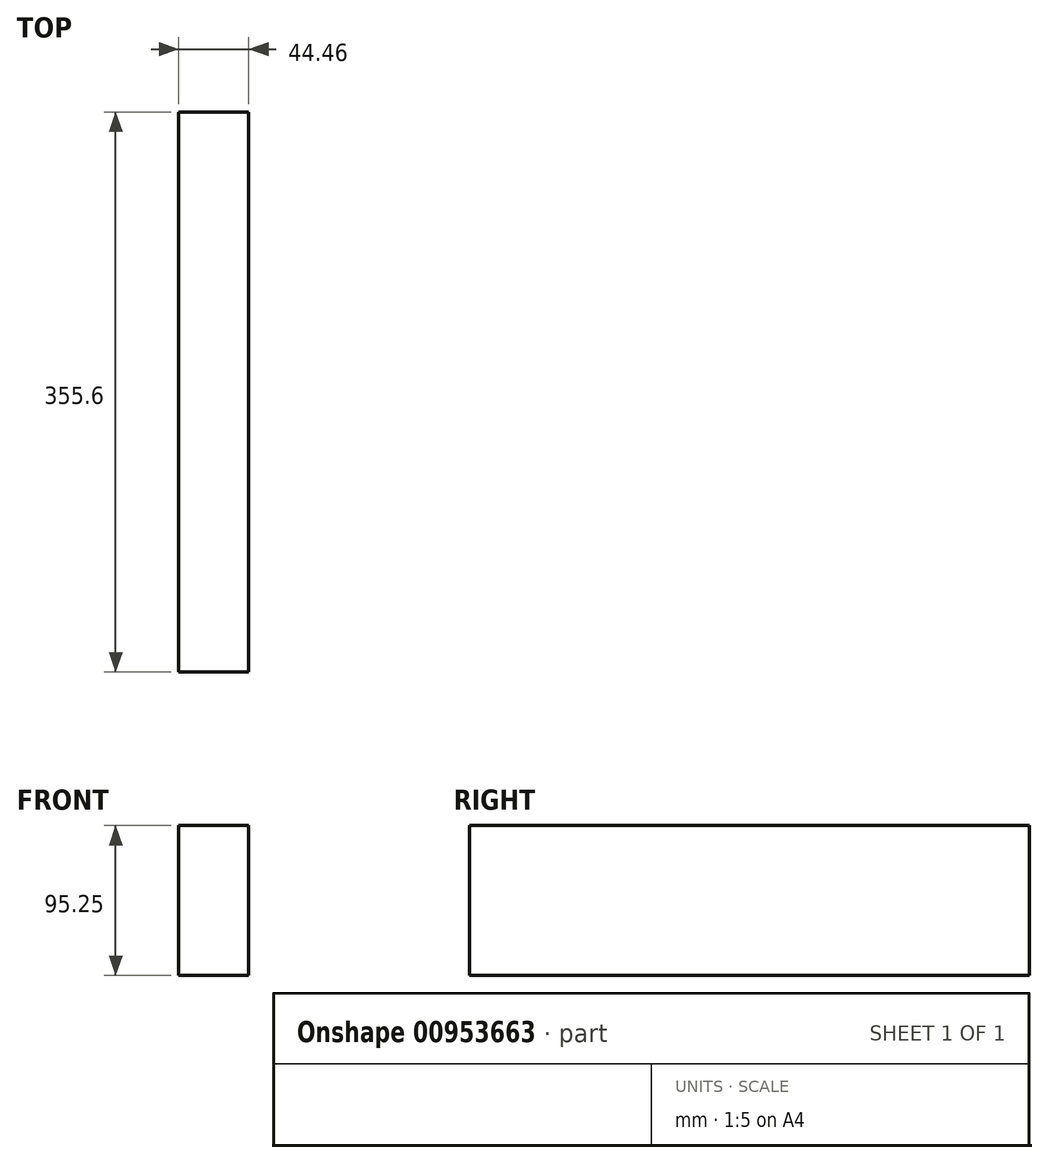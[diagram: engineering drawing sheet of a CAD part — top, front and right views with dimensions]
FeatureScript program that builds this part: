
annotation { "Feature Type Name" : "Feature", "Feature Type Description" : "" }
export const myFeature = defineFeature(function(context is Context, id is Id, definition is map)
    precondition{}
    {
        {
            var Q0;
            Q0=qCreatedBy(makeId("Top.planeOp"),FACE);
            var sketch = newSketch(context, id + "F0", { "sketchPlane" : qUnion([Q0])});
            skLineSegment(sketch, "E0.bottom", {"start": v(22.22, -177.8) * mm, "end": v(-22.23, -177.8) * mm});
            skLineSegment(sketch, "E0.top", {"start": v(22.23, 177.8) * mm, "end": v(-22.23, 177.8) * mm});
            skLineSegment(sketch, "E0.left", {"start": v(22.22, -177.8) * mm, "end": v(22.22, 177.8) * mm});
            skLineSegment(sketch, "E0.right", {"start": v(-22.23, -177.8) * mm, "end": v(-22.23, 177.8) * mm});
            skPoint(sketch, "E0.middle", {"position": v(0, 0) * mm});
            skSolve(sketch);
        }
        {
            var Q0;
            Q0=makeQuery(id+"F0.imprint","IMPRINT",FACE,{"disambiguationData":[TD([[makeQuery(id+"F0.imprint","IMPRINT",EDGE,{"derivedFrom":sQuery(id+"F0.wireOp",EDGE,"E0.bottom")}),-1.0]])]});
            extrude(context, id + "F1", {"entities" : qUnion([Q0]), "depth" : 95.25 * mm, "offsetDistance" : 25.4 * mm});
        }
    });
